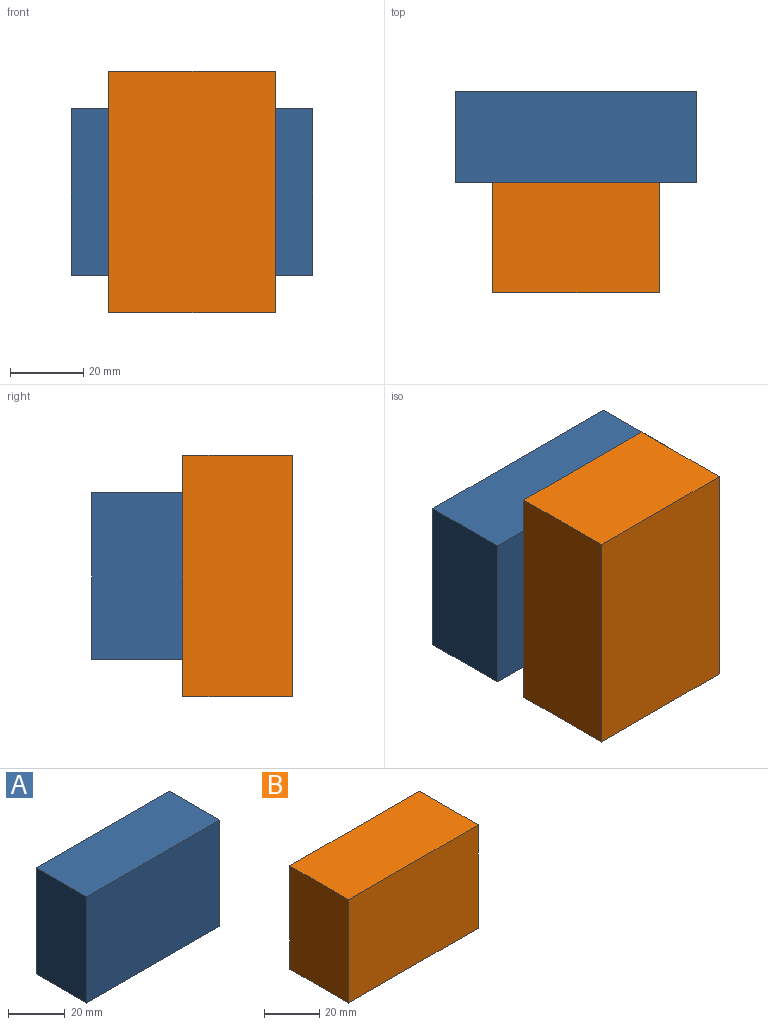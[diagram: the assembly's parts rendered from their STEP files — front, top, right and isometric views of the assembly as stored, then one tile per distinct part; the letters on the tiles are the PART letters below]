
ASSEMBLY  parts=2 mates=1
PART A: 6 faces, bbox 66.2x25x45.6 mm
  f0: plane 66.15x25mm, normal (0,0,1), area 1653.8mm2, adj f1,f3,f4,f5
  f1: plane 45.63x25mm, normal (-1,0,0), area 1140.7mm2, adj f0,f2,f4,f5
  f2: plane 66.15x25mm, normal (0,0,-1), area 1653.8mm2, adj f1,f3,f4,f5
  f3: plane 45.63x25mm, normal (1,0,0), area 1140.7mm2, adj f0,f2,f4,f5
  f4: plane 66.15x45.63mm, normal (0,-1,0), area 3018.5mm2, adj f0,f1,f2,f3
  f5: plane 66.15x45.63mm, normal (0,1,0), area 3018.5mm2, adj f0,f1,f2,f3
PART B: 6 faces, bbox 66.2x30x45.6 mm
  f0: plane 45.63x30mm, normal (-1,0,0), area 1368.9mm2, adj f1,f3,f4,f5
  f1: plane 66.15x30mm, normal (0,0,-1), area 1984.6mm2, adj f0,f2,f4,f5
  f2: plane 45.63x30mm, normal (1,0,0), area 1368.9mm2, adj f1,f3,f4,f5
  f3: plane 66.15x30mm, normal (0,0,1), area 1984.6mm2, adj f0,f2,f4,f5
  f4: plane 66.15x45.63mm, normal (0,-1,0), area 3018.5mm2, adj f0,f1,f2,f3
  f5: plane 66.15x45.63mm, normal (0,1,0), area 3018.5mm2, adj f0,f1,f2,f3
PLACE A t=(68.45,25.1,-5.75)mm
PLACE B rot(axis=(0.71,0,0.71),180deg) t=(-26.68,-29.8,26.68)mm
MATE fastened B.f4 <-> A.f4  axis (0,1,0) through (-26.07,0.1,0.61)mm
